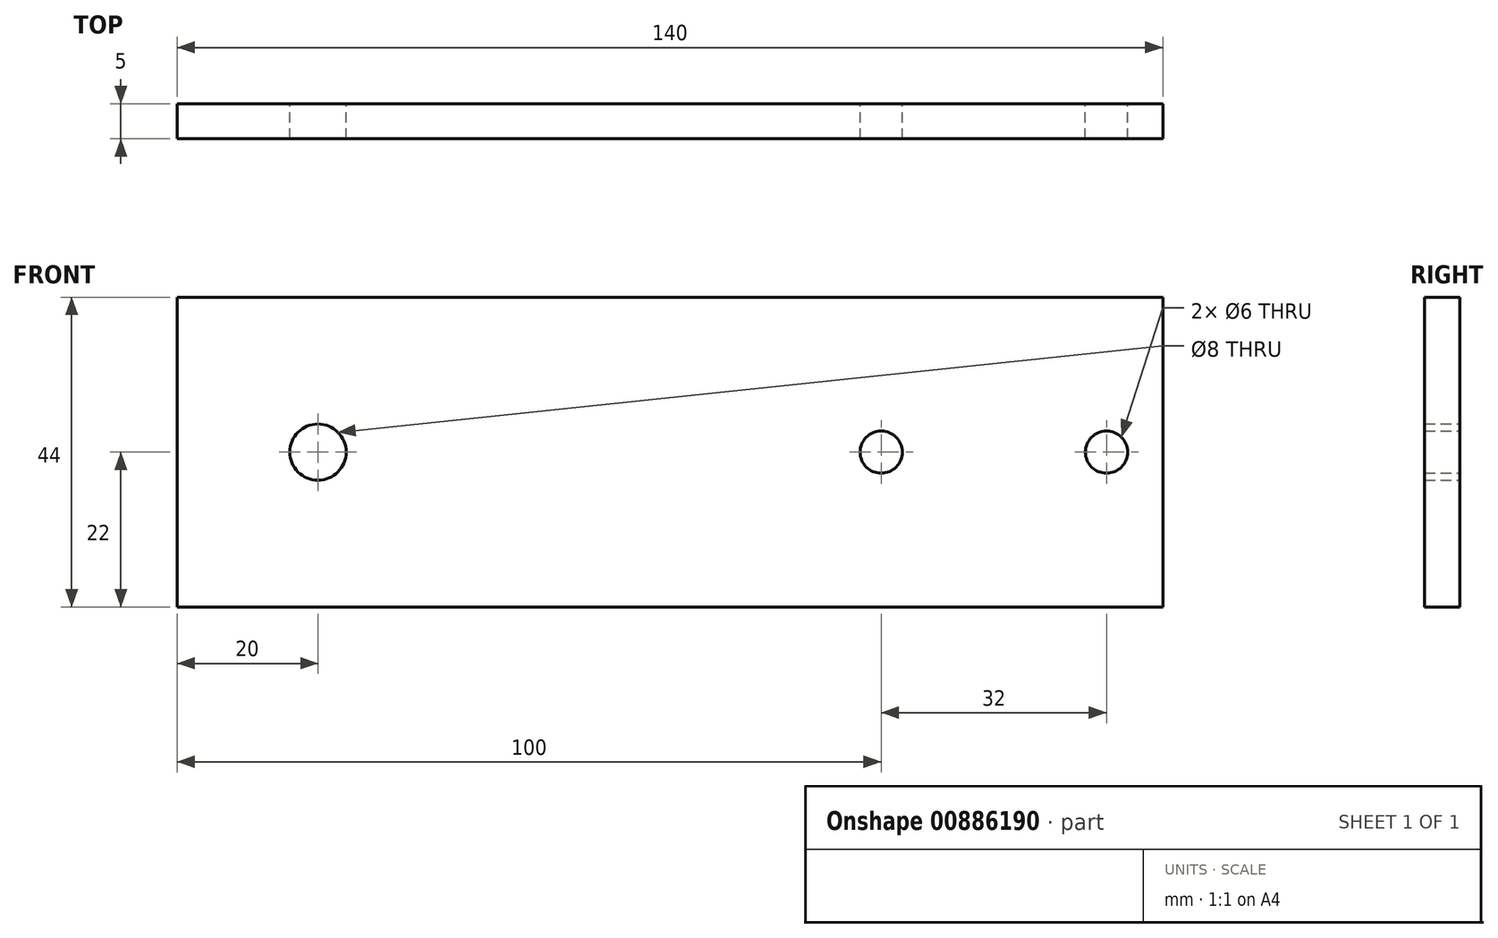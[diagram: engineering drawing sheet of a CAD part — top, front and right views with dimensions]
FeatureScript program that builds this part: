
annotation { "Feature Type Name" : "Feature", "Feature Type Description" : "" }
export const myFeature = defineFeature(function(context is Context, id is Id, definition is map)
    precondition{}
    {
        {
            var Q0;
            Q0=qCreatedBy(makeId("Front.planeOp"),FACE);
            var sketch = newSketch(context, id + "F0", { "sketchPlane" : qUnion([Q0])});
            skLineSegment(sketch, "E0.bottom", {"start": v(0, 0) * mm, "end": v(-140, 0) * mm});
            skLineSegment(sketch, "E0.top", {"start": v(0, 44) * mm, "end": v(-140, 44) * mm});
            skLineSegment(sketch, "E0.left", {"start": v(0, 0) * mm, "end": v(0, 44) * mm});
            skLineSegment(sketch, "E0.right", {"start": v(-140, 0) * mm, "end": v(-140, 44) * mm});
            skLineSegment(sketch, "E1.left", {"start": v(6.83, 16.52) * mm, "end": v(6.83, 16.52) * mm});
            skLineSegment(sketch, "E1.right", {"start": v(3.62, 16.52) * mm, "end": v(3.62, 16.52) * mm});
            skCircle(sketch, "E2", {"center": v(-120, 22) * mm, "radius": 4 * mm});
            skLineSegment(sketch, "E3", {"start": v(-120, 22) * mm, "end": v(-22.8, 22) * mm, "construction": true});
            skCircle(sketch, "E4", {"center": v(-8, 22) * mm, "radius": 3 * mm});
            skCircle(sketch, "E5", {"center": v(-40, 22) * mm, "radius": 3 * mm});
            skSolve(sketch);
        }
        {
            var Q0;
            Q0=makeQuery(id+"F0.imprint","IMPRINT",FACE,{"disambiguationData":[TD([[makeQuery(id+"F0.imprint","IMPRINT",EDGE,{"derivedFrom":sQuery(id+"F0.wireOp",EDGE,"E0.bottom")}),-1.0]])]});
            extrude(context, id + "F1", {"entities" : qUnion([Q0]), "depth" : 5 * mm, "offsetDistance" : 25 * mm});
        }
    });
